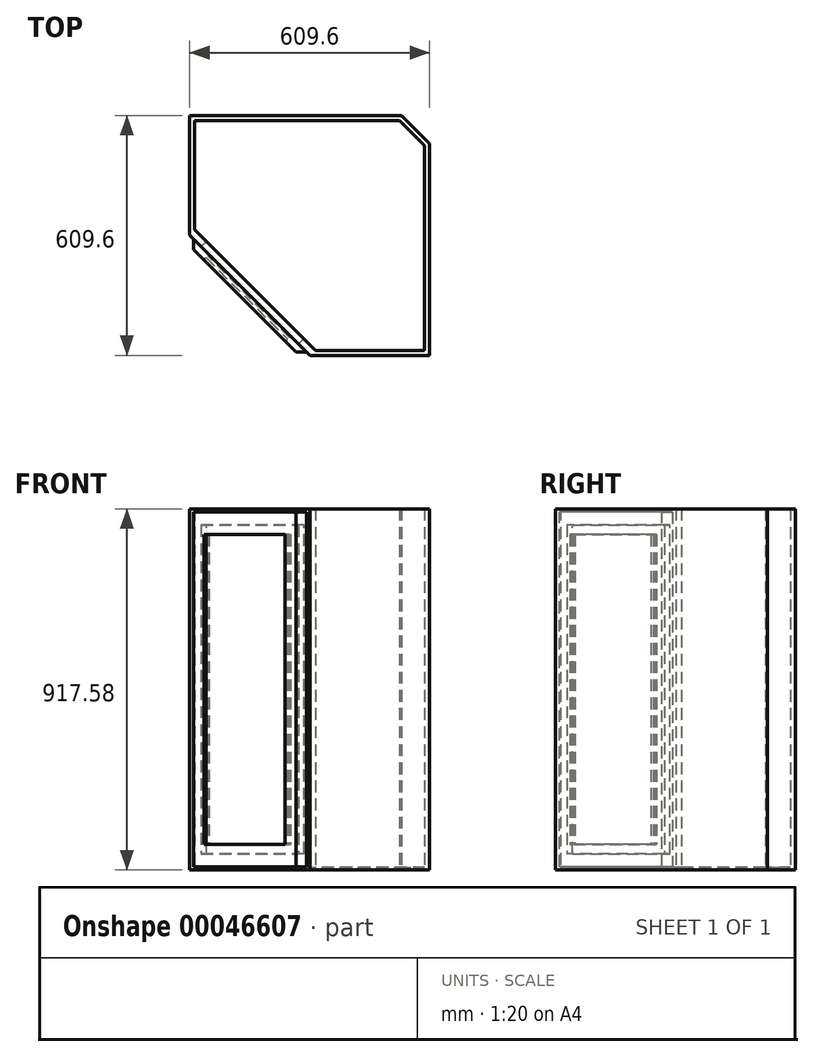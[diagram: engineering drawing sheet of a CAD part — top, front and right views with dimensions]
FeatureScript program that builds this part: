
annotation { "Feature Type Name" : "Feature", "Feature Type Description" : "" }
export const myFeature = defineFeature(function(context is Context, id is Id, definition is map)
    precondition{}
    {
        {
            var Q0;
            Q0=qCreatedBy(makeId("Top.planeOp"),FACE);
            var sketch = newSketch(context, id + "F0", { "sketchPlane" : qUnion([Q0])});
            skLineSegment(sketch, "E0.bottom", {"start": v(-304.8, 304.8) * mm, "end": v(304.8, 304.8) * mm, "construction": true});
            skLineSegment(sketch, "E0.top", {"start": v(-304.8, -304.8) * mm, "end": v(304.8, -304.8) * mm, "construction": true});
            skLineSegment(sketch, "E0.left", {"start": v(-304.8, 304.8) * mm, "end": v(-304.8, -304.8) * mm, "construction": true});
            skLineSegment(sketch, "E0.right", {"start": v(304.8, 304.8) * mm, "end": v(304.8, -304.8) * mm, "construction": true});
            skLineSegment(sketch, "E1", {"start": v(-304.8, 304.8) * mm, "end": v(304.8, -304.8) * mm, "construction": true});
            skLineSegment(sketch, "E2", {"start": v(-304.8, 0.53) * mm, "end": v(0.53, -304.8) * mm, "construction": true});
            skLineSegment(sketch, "E3", {"start": v(232.96, 304.8) * mm, "end": v(304.8, 232.96) * mm, "construction": true});
            skSolve(sketch);
        }
        {
            var Q0;
            Q0=qCreatedBy(makeId("Top.planeOp"),FACE);
            var sketch = newSketch(context, id + "F1", { "sketchPlane" : qUnion([Q0])});
            skLineSegment(sketch, "E4", {"start": v(-304.8, 0.53) * mm, "end": v(0.53, -304.8) * mm});
            skLineSegment(sketch, "E5", {"start": v(-304.8, 0.53) * mm, "end": v(-304.8, 27.47) * mm});
            skLineSegment(sketch, "E6", {"start": v(0.53, -304.8) * mm, "end": v(27.47, -304.8) * mm});
            skLineSegment(sketch, "E7", {"start": v(-304.8, 27.47) * mm, "end": v(27.47, -304.8) * mm});
            skLineSegment(sketch, "E8", {"start": v(-304.8, 27.47) * mm, "end": v(-304.8, 304.8) * mm});
            skLineSegment(sketch, "E9", {"start": v(27.47, -304.8) * mm, "end": v(304.8, -304.8) * mm});
            skLineSegment(sketch, "E10", {"start": v(304.8, -304.8) * mm, "end": v(304.8, 232.96) * mm});
            skLineSegment(sketch, "E11", {"start": v(-304.8, 304.8) * mm, "end": v(232.96, 304.8) * mm});
            skLineSegment(sketch, "E12", {"start": v(232.96, 304.8) * mm, "end": v(304.8, 232.96) * mm});
            skLineSegment(sketch, "E13", {"start": v(-292.1, 14.77) * mm, "end": v(-292.1, 292.1) * mm});
            skLineSegment(sketch, "E14", {"start": v(-292.1, 292.1) * mm, "end": v(227.7, 292.1) * mm});
            skLineSegment(sketch, "E15", {"start": v(227.7, 292.1) * mm, "end": v(292.1, 227.7) * mm});
            skLineSegment(sketch, "E16", {"start": v(292.1, 227.7) * mm, "end": v(292.1, -292.1) * mm});
            skLineSegment(sketch, "E17", {"start": v(292.1, -292.1) * mm, "end": v(14.77, -292.1) * mm});
            skSolve(sketch);
        }
        {
            var Q0;
            Q0=makeQuery(id+"F1.imprint","IMPRINT",FACE,{"disambiguationData":[TD([[makeQuery(id+"F1.imprint","IMPRINT",EDGE,{"derivedFrom":sQuery(id+"F1.wireOp",EDGE,"E4")}),1.0]])]});
            var Q1;
            {var subQ1=sQuery(id+"F1.wireOp",EDGE,"E8");Q1=makeQuery(id+"F1.imprint","IMPRINT",FACE,{"disambiguationData":[TD([[makeQuery(id+"F1.imprint","IMPRINT",EDGE,{"derivedFrom":subQ1}),-1.0]])]});}
            extrude(context, id + "F2", {"entities" : qUnion([Q0, Q1]), "depth" : 917.57 * mm});
        }
        {
            var Q0;
            {var subQ0=sQuery(id+"F1.wireOp",EDGE,"E4");Q0=makeQuery(id+"FLCiGweJVPZvpob_1.boolean.opBoolean","MERGE",FACE,{"derivedFrom":[makeQuery(id+"F2.opExtrude","SWEPT_FACE",FACE,{"disambiguationData":[OSD([subQ0])]}),makeQuery(id+"FLCiGweJVPZvpob_1.opExtrude","SWEPT_FACE",FACE,{"disambiguationData":[OSD([subQ0])]})]});}
            var sketch = newSketch(context, id + "F3", { "sketchPlane" : qUnion([Q0])});
            skLineSegment(sketch, "E18.bottom", {"start": v(-174.63, 876.3) * mm, "end": v(174.62, 876.3) * mm});
            skLineSegment(sketch, "E18.top", {"start": v(-174.62, 41.28) * mm, "end": v(174.63, 41.28) * mm});
            skLineSegment(sketch, "E18.left", {"start": v(-174.62, 876.3) * mm, "end": v(-174.62, 41.28) * mm});
            skLineSegment(sketch, "E18.right", {"start": v(174.62, 876.3) * mm, "end": v(174.63, 41.28) * mm});
            skSolve(sketch);
        }
        {
            var Q0;
            Q0=qSketchRegion(id+"F3",true);
            var Q1;
            Q1=makeQuery(id+"F3.imprint","IMPRINT",FACE,{"disambiguationData":[TD([[makeQuery(id+"F3.imprint","IMPRINT",EDGE,{"derivedFrom":sQuery(id+"F3.wireOp",EDGE,"E18.bottom")}),-1.0]])]});
            extrude(context, id + "F4", {"entities" : qUnion([Q0, Q1]), "operationType" : NewBodyOperationType.REMOVE, "oppositeDirection" : true, "depth" : 25.4 * mm});
        }
        {
            var Q0;
            {var subQ0=sQuery(id+"F1.wireOp",EDGE,"E4");Q0=makeQuery(id+"FLCiGweJVPZvpob_1.boolean.opBoolean","MERGE",FACE,{"derivedFrom":[makeQuery(id+"F2.opExtrude","SWEPT_FACE",FACE,{"disambiguationData":[OSD([subQ0])]}),makeQuery(id+"FLCiGweJVPZvpob_1.opExtrude","SWEPT_FACE",FACE,{"disambiguationData":[OSD([subQ0])]})]});}
            var sketch = newSketch(context, id + "F5", { "sketchPlane" : qUnion([Q0])});
            skLineSegment(sketch, "E19.bottom", {"start": v(-203.2, 909.64) * mm, "end": v(203.2, 909.64) * mm});
            skLineSegment(sketch, "E19.top", {"start": v(-203.2, 7.94) * mm, "end": v(203.2, 7.94) * mm});
            skLineSegment(sketch, "E19.left", {"start": v(-203.2, 909.64) * mm, "end": v(-203.2, 7.94) * mm});
            skLineSegment(sketch, "E19.right", {"start": v(203.2, 909.64) * mm, "end": v(203.2, 7.94) * mm});
            skLineSegment(sketch, "E20.bottom", {"start": v(-146.05, 852.49) * mm, "end": v(146.05, 852.49) * mm});
            skLineSegment(sketch, "E20.top", {"start": v(-146.05, 65.09) * mm, "end": v(146.05, 65.09) * mm});
            skLineSegment(sketch, "E20.left", {"start": v(-146.05, 852.49) * mm, "end": v(-146.05, 65.09) * mm});
            skLineSegment(sketch, "E20.right", {"start": v(146.05, 852.49) * mm, "end": v(146.05, 65.09) * mm});
            skSolve(sketch);
        }
        {
            var Q0;
            Q0=qSketchRegion(id+"F5",true);
            extrude(context, id + "F6", {"entities" : qUnion([Q0]), "depth" : 19.05 * mm});
        }
        {
            var Q0;
            Q0=makeQuery(id+"F6.opExtrude","SWEPT_FACE",FACE,{"disambiguationData":[OSD([sQuery(id+"F5.wireOp",EDGE,"E19.bottom")])]});
            var sketch = newSketch(context, id + "F7", { "sketchPlane" : qUnion([Q0])});
            skLineSegment(sketch, "E21", {"start": v(-8.45, -295.82) * mm, "end": v(-35.4, -295.82) * mm});
            skLineSegment(sketch, "E22", {"start": v(-8.45, -295.82) * mm, "end": v(-21.92, -309.3) * mm});
            skLineSegment(sketch, "E23", {"start": v(-21.92, -309.3) * mm, "end": v(-35.4, -295.82) * mm});
            skLineSegment(sketch, "E24", {"start": v(-295.82, -8.45) * mm, "end": v(-309.3, -21.92) * mm});
            skLineSegment(sketch, "E25", {"start": v(-309.3, -21.92) * mm, "end": v(-295.82, -35.4) * mm});
            skLineSegment(sketch, "E26", {"start": v(-295.82, -35.4) * mm, "end": v(-295.82, -8.45) * mm});
            skSolve(sketch);
        }
        {
            var Q0;
            Q0=qSketchRegion(id+"F7",true);
            extrude(context, id + "F8", {"entities" : qUnion([Q0]), "operationType" : NewBodyOperationType.REMOVE, "endBound" : BoundingType.THROUGH_ALL, "oppositeDirection" : true, "depth" : 25.4 * mm});
        }
        {
            var Q0;
            Q0=makeQuery(id+"F6.opExtrude","SWEPT_FACE",FACE,{"disambiguationData":[OSD([sQuery(id+"F5.wireOp",EDGE,"E20.top")])]});
            var sketch = newSketch(context, id + "F9", { "sketchPlane" : qUnion([Q0])});
            skLineSegment(sketch, "E27", {"start": v(-258.78, -52.23) * mm, "end": v(-263.27, -56.72) * mm});
            skLineSegment(sketch, "E28", {"start": v(-52.23, -258.78) * mm, "end": v(-56.72, -263.27) * mm});
            skLineSegment(sketch, "E29", {"start": v(-52.23, -258.78) * mm, "end": v(-258.78, -52.23) * mm});
            skLineSegment(sketch, "E30", {"start": v(-263.27, -56.72) * mm, "end": v(-56.72, -263.27) * mm});
            skSolve(sketch);
        }
        {
            var Q0;
            Q0=qSketchRegion(id+"F9",true);
            extrude(context, id + "F10", {"entities" : qUnion([Q0]), "operationType" : NewBodyOperationType.ADD, "endBound" : BoundingType.UP_TO_NEXT, "depth" : 25.4 * mm});
        }
        {
            var Q0;
            {var subQ0=sQuery(id+"F1.wireOp",EDGE,"E13");Q0=makeQuery(id+"F1.imprint","IMPRINT",FACE,{"disambiguationData":[TD([[makeQuery(id+"F1.imprint","IMPRINT",EDGE,{"derivedFrom":subQ0}),-1.0]])]});}
            extrude(context, id + "F11", {"entities" : qUnion([Q0]), "operationType" : NewBodyOperationType.ADD, "depth" : 6.35 * mm});
        }
    });
